# Revit family: QF_BPRO_BPT E 2 x 18 duo H_N_575209
name_source: partatom
category: Sonderausstattung
revit_build: Autodesk Revit 2018 (Build: 20181015_0930(x64)
units: mm (PartAtom-declared; Revit-internal decimal feet)

## family parameters
Arbeitsebenenbasiert = Nein
Beim Laden mit Abzugskörper schneiden = Nein
Bemaßung runder Anschluss = Durchmesser verwenden
Gemeinsam genutzt = Nein
Immer vertikal = Ja
Raumberechnungspunkt = Nein
Teiletyp = Normal

## types (1)
- BPT E 2 x 18 duo H/N
    Accessory = Ja
    Beschreibung = BPT E 2 x 18 duo heated / neutral
2-compartment B.PROTHERM E food
transport container made of stainless steel,
mobile, synthetic castors, corrosion-resistant in
compliance with DIN 18867-8, castors 125 mm
dia., 2 fixed and 2 steering castors, 2 of which
have brakes,
left compartment: convection-heated,
temperature range: +30 °C to +95 °C,
right compartment: neutral
    CE Approved = Ja
    Conn Conduit = Ja
    Conn Plug = Schuko plug
    Cycle = 50 Hz
    Depth Actual = 821 mm  [stored 2.69357 ft]
    Electric power = 800 W
    Foodservice Equipment Identifier = Ja
    Height Actual = 1072 mm
    Hersteller = B.PRO GmbH
    Item Number = 575209
    Kosten = 5800 $
    Length Actual = 1026 mm  [stored 3.36614 ft]
    Main switch integrated = Ja
    Masterspec = Dimensions

Length:				 1026 mm
Width:			   821 mm
Height:			 1072 mm

Model

Design
The B.PROTHERM is made of AISI 304 stainless steel. The surface is micro-polished.  
Body and hinged doors are double-walled and fitted with CFC-free PUR foam panels for thermal insulation. As a duo model, the trolley features two separate, thermally insulated compartments side by side.
The left compartment is convection-heated while the right compartment has a neutral design.
The B.PROTHERM is mobile thanks to corrosion-resistant synthetic castors as per DIN 18867, Part 8 (2 fixed and 2 steering castors with brakes, castor diameter 125 mm). The sturdy, synthetic base structure with integrated all-round bumper rail protects the unit and furniture from damage.

Body
The base and rear and side walls are fitted with all-round edge radius R2 and are spot-welded at their points of contact (hygienic type HS). The interior is fully equipped with 18 pairs of deep-drawn stainless steel ledge walls per compartment for easy cleaning and maximum hygiene. The support ledges have a uniform spacing of 38.3 mm to hold Gastronorm containers size GN 1/1 or their subdivisions. This means all common spacing dimensions (about 75 mm, 115 mm) can be housed in a single unit and ensures efficient use of the interior. 

The heating module with convection heating is permanently fitted into the heated compartment's rear panel. Control range: +30 °C to +95 °C. The temperature can be regulated down to the degree.   
There is an air baffle in front of the heating module on the rear panel in the interior body. This ensures optimum, rapid, uniform air circulation throughout the interior and also serves as a stop for inserted GN containers. The air baffle can be removed for cleaning purposes. 
Interior and exterior body are vertically connected with synthetic profiles and thermally separated.

The B.PROTHERM is fitted with 2 horizontal push handles on the left and right short sides as standard. The ergonomic positioning of the handles makes the trolley easy to manoeuvre. 
The push handles are inside the bumper rail. The helix cord and plug holder are attached on the unit rear and also within the all-round bumper rail.

The B.PRO control is integrated into the top of the unit, making it easy to use. It contains the unit on/off button, a menu button, a function button and an up/down button, e.g. to regulate the temperature in the interior precisely. 

Doors
The trolley is equipped with two doors on its front that can be opened 270° and features a lock on its bottom plate. The doors are inside the bumper rail when open or closed and are thus protected from damage. The push handles are still accessible when the door is open. The robust door hinges are made of stainless steel investment casting. The hinge design eliminates risk of injury if a user should accidentally take hold of the hinge. A ventilation flap is fitted into the door on the convection-heated compartment to regulate moisture in the container interior.
The doors are also fitted with an all-round, food-safe seal (TPE) that closes against the trolley body and can be removed. 

The doors are fitted with a 2-point locking system. It is easy to open from the outside by simply pushing up the door handle. 
The B.PROTHERM has a push-button which glows in the dark in its interior. The patented panic opening can be identified if someone should get accidentally locked inside the interior and the door lock can be unlocked from the inside by pressing the button. What is known as the afterglow effect meets the requirements for safety-relevant components specified in ISO 16069. 

 
Options

•	Can be customised with powder coating on body and doors in 12 colours
•	Digitisation/connectivity for digital hygiene, temperature and process management using optionally built-in sensor technology 
•	Additional socket on rear panel (instead of plug holder) for coupling additional units
•	Top with stainless steel railing on 3 sides
•	Top with stainless steel railing on 4 sides
•	Hygienic type H1
•	Door, lockable
•	Convenient door opening with foot operation
•	Stainless-steel castors, 125 mm in diameter, 2 fixed and 2 steering castors with brakes 
•	Anti-static castors, 125 mm in diameter, 2 fixed and 2 steering castors with brakes, corrosion-resistant in compliance with DIN 18867-8, synthetic
•	Galvanised steel castors, 160 mm in diameter, 2 fixed and 2 steering castors with brakes 
•	Galvanised steel castors with elastic tyres, 160 mm in diameter, 2 fixed and 2 steering castors with brakes 
•	Stainless-steel castors, 160 mm in diameter, 2 fixed and 2 steering castors with brakes 
•	Stainless-steel castors with elastic tyres, 160 mm in diameter, 2 fixed and 2 steering castors with brake 

Accessories

•	Thermal separation element for the neutral compartment to sub-divide the interior to allow use of different temperature zones
•	Eutectic plate -3 °C, synthetic 
(Order no.: 568 136)
•	Eutectic plate -12 °C, synthetic 
(Order no.: 573 332)
•	Slide-in frame to sub-divide GN containers
with max. depth 150 mm (order no. 564 352)
•	GN support bars for variable insertion of GN containers of the size GN 1/4, GN 1/6, GN 1/9 in the slide-in frame (ST 3 order no. 550 650; ST 5 order no. 550 651)
•	Menu card holder for the door on front, stainless steel, to attach DIN A5 and DIN A6 menu cards (order no. 575 230)
•	BPT E menu card, DIN A6 (order no. 564 353) 
•	Special pen for marking BPT E menu cards (order no. 564 361)
•	Menu card box, synthetic (order no. 564 355)

Technical data

Material:	Stainless steel,
	synthetic
Insulating material:		PUR foam panels, CFC-free 
Weight:	110 kg
Capacity:	9 x GN 1/1-65 per compartment
	2 x 18 pairs of deep-drawn support ledges
	Space between ledges of 38.3 mm
Protection type: 	IPX5
Connected load:	220–240 V AC/50–60 Hz/ 
	0.8 kW
Temperature range:	+30 °C to +95 °C*
Emissions:	The workplace-specific noise level for the unit is less than 70 dB(A)
* Measured at the container's geometrical centre

Special features

•	Two thermally separated compartments for different temperature ranges 
•	Extremely efficient, flexible use of interior thanks to uniform space between ledges of 38.3 mm
•	Deep-drawn stainless steel ledge walls for easy cleaning and maximum hygiene.
•	Sturdy, enclosed, solid, synthetic base structure with integrated all-round bumper rail.
•	Hinged door with door opening of 270°, with lock 
•	Optional connectivity function 

Make

Manufacturer:			B.PRO
Model:	BPT E 2 x 18 duo H/N
	B.PROTHERM
Order no.			575 209
    Material = QF_Metal-Stainless-Steel_general
    Material Rollen = QF_Plastic-Dark_Grey-Matt
    Material Stoßschutz = QF_Plastic-Black-Matt
    Model Warning = Transport:
Transport the unit in an upright position only.
Transport with a truck or delivery vehicle
The unit may only be transported in a truck or delivery vehicle which features a loading ramp.
The loading ramp must not exceed an angle of inclination of 10°.
The unit is not properly secured for transport if only the castor brakes have been applied.
Secure the unit on all four sides to prevent it from shifting.
Secure the unit against vertical movement during transport.
Use padded locking bars.

Loading and removing food:
To prevent extension of the centre of gravity to the unit top, load unit from the bottom up when
loading partially.
Food is removed from the top downwards.
Do not exceed the upper weight limit specified in the technical data when loading.
Always cover food on plates with cloches. Always cover Gastronorm containers containing food
with lids. Gastronorm containers placed in the unit must be able to withstand a temperature of at
least +100 °C. Polycarbonate Gastronorm containers must not be used, for example.
To prevent shifting of the centre of gravity to the unit top, the unit should generally be loaded
from the bottom up. Fully load the ledges, with two Gastronorm containers GN 1/1 on each
ledge, for example, so that the containers won't slide when changing locations.
Hot steam:
There is a risk that hot steam can escape and cause scalding if the unit door is opened while
keeping food hot.
Do not hold body parts in or over the opening area when opening the door.

Detailed safety information can be found in the operating instructions.
    Modell = BPT E 2 x 18 duo H/N
    Sound Level = < 70 dB(A)
    Typenkommentare = food transport container convection-heated and neutral
    URL = https://www.bpro-solutions.com
    URL Manufacturer = https://www.bpro-solutions.com
    URL Recommended Spares List = https://www.bpro-solutions.com
    Volts = 220 V
    Weight = 110.00 kg

note: [stored X ft] marks values corroborated as IEEE doubles in the binary element streams (Revit-internal decimal feet)
